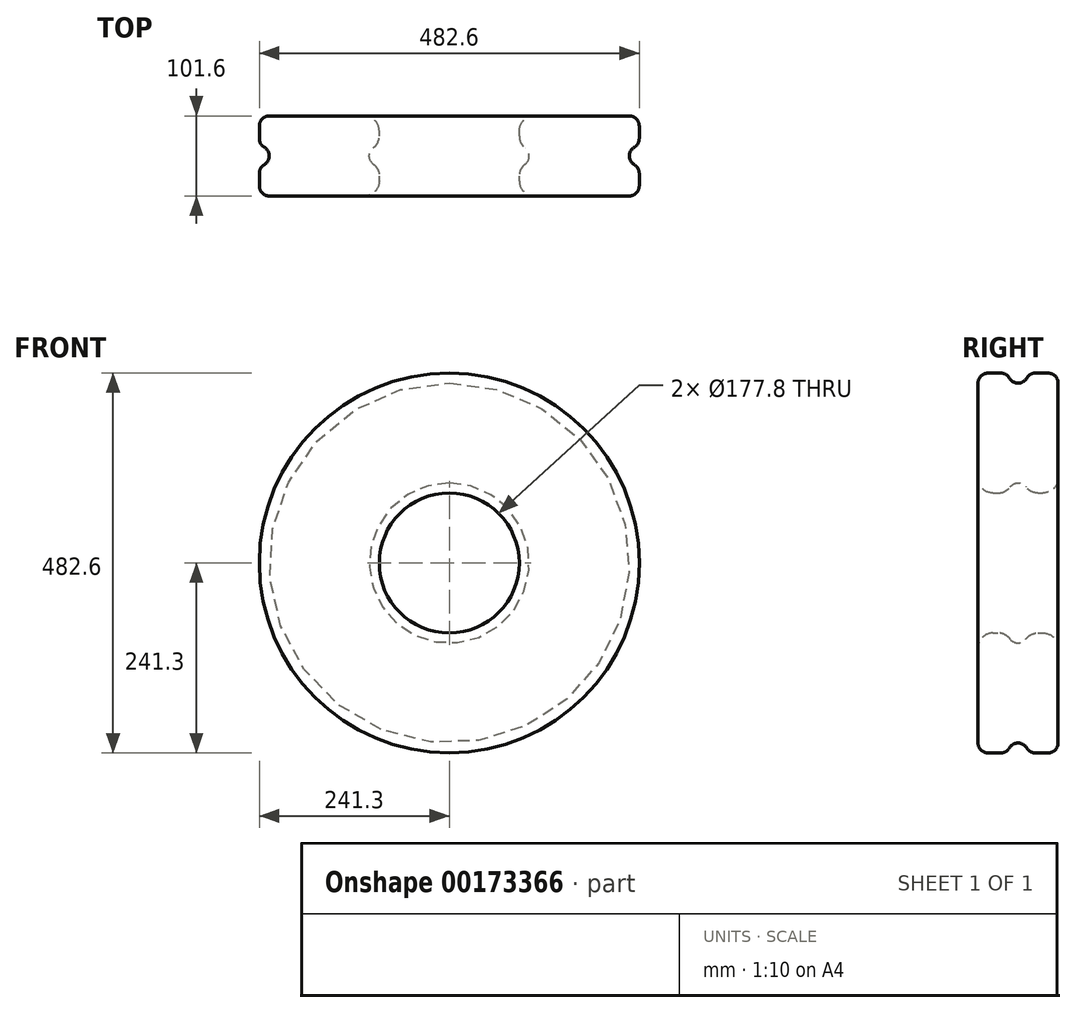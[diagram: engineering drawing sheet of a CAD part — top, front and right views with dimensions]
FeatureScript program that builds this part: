
annotation { "Feature Type Name" : "Feature", "Feature Type Description" : "" }
export const myFeature = defineFeature(function(context is Context, id is Id, definition is map)
    precondition{}
    {
        {
            var Q0;
            Q0=qCreatedBy(makeId("Top.planeOp"),FACE);
            var sketch = newSketch(context, id + "F0", { "sketchPlane" : qUnion([Q0])});
            skLineSegment(sketch, "E0.bottom", {"start": v(88.9, 0) * mm, "end": v(241.3, 0) * mm});
            skLineSegment(sketch, "E0.top", {"start": v(88.9, 101.6) * mm, "end": v(241.3, 101.6) * mm});
            skLineSegment(sketch, "E0.left", {"start": v(88.9, 0) * mm, "end": v(88.9, 38.1) * mm});
            skLineSegment(sketch, "E0.right", {"start": v(241.3, 0) * mm, "end": v(241.3, 38.1) * mm});
            skLineSegment(sketch, "E1", {"start": v(101.6, 50.8) * mm, "end": v(228.6, 50.8) * mm});
            skLineSegment(sketch, "E2", {"start": v(88.9, 38.1) * mm, "end": v(241.3, 38.1) * mm});
            skLineSegment(sketch, "E3", {"start": v(88.9, 63.5) * mm, "end": v(241.3, 63.5) * mm});
            skLineSegment(sketch, "E4", {"start": v(0, 107.57) * mm, "end": v(0, 0) * mm, "construction": true});
            skArc(sketch, "E5", {"start": v(88.9, 38.1) * mm, "mid": v(101.6, 50.8) * mm, "end": v(88.9, 63.5) * mm});
            skArc(sketch, "E6", {"start": v(241.3, 63.5) * mm, "mid": v(228.6, 50.8) * mm, "end": v(241.3, 38.1) * mm});
            skLineSegment(sketch, "E7.trimOffspring", {"start": v(88.9, 63.5) * mm, "end": v(88.9, 101.6) * mm});
            skLineSegment(sketch, "E8.trimOffspring", {"start": v(241.3, 63.5) * mm, "end": v(241.3, 101.6) * mm});
            skSolve(sketch);
        }
        {
            var Q0;
            Q0 = qSketchRegion(id + "F0", true);
            var Q1;
            Q1=sQuery(id+"F0.wireOp",EDGE,"E4");
            revolve(context, id + "F1", {"entities" : qUnion([Q0]), "axis" : qUnion([Q1]), "revolveType" : RevolveType.FULL});
        }
        {
            var Q0;
            Q0=makeQuery(id+"F1.opRevolve","SWEPT_EDGE",EDGE,{"disambiguationData":[OSD([sQuery(id+"F0.wireOp",EDGE,"E3"),sQuery(id+"F0.wireOp",EDGE,"E6"),sQuery(id+"F0.wireOp",EDGE,"E8.trimOffspring")])]});
            var Q1;
            Q1=makeQuery(id+"F1.opRevolve","SWEPT_EDGE",EDGE,{"disambiguationData":[OSD([sQuery(id+"F0.wireOp",EDGE,"E0.top"),sQuery(id+"F0.wireOp",EDGE,"E8.trimOffspring")])]});
            var Q2;
            Q2=makeQuery(id+"F1.opRevolve","SWEPT_EDGE",EDGE,{"disambiguationData":[OSD([sQuery(id+"F0.wireOp",EDGE,"E0.right"),sQuery(id+"F0.wireOp",EDGE,"E2"),sQuery(id+"F0.wireOp",EDGE,"E6")])]});
            var Q3;
            Q3=makeQuery(id+"F1.opRevolve","SWEPT_EDGE",EDGE,{"disambiguationData":[OSD([sQuery(id+"F0.wireOp",EDGE,"E0.bottom"),sQuery(id+"F0.wireOp",EDGE,"E0.right")])]});
            fillet(context, id + "F2", {"entities" : qUnion([Q0, Q1, Q2, Q3]), "radius" : 12.7 * mm, "tangentPropagation" : true, "allowEdgeOverflow" : false});
        }
        {
            var Q0;
            Q0=makeQuery(id+"F1.opRevolve","SWEPT_EDGE",EDGE,{"disambiguationData":[OSD([sQuery(id+"F0.wireOp",EDGE,"E0.top"),sQuery(id+"F0.wireOp",EDGE,"E7.trimOffspring")])]});
            var Q1;
            Q1=makeQuery(id+"F1.opRevolve","SWEPT_EDGE",EDGE,{"disambiguationData":[OSD([sQuery(id+"F0.wireOp",EDGE,"E3"),sQuery(id+"F0.wireOp",EDGE,"E5"),sQuery(id+"F0.wireOp",EDGE,"E7.trimOffspring")])]});
            var Q2;
            Q2=makeQuery(id+"F1.opRevolve","SWEPT_EDGE",EDGE,{"disambiguationData":[OSD([sQuery(id+"F0.wireOp",EDGE,"E0.left"),sQuery(id+"F0.wireOp",EDGE,"E2"),sQuery(id+"F0.wireOp",EDGE,"E5")])]});
            var Q3;
            Q3=makeQuery(id+"F1.opRevolve","SWEPT_EDGE",EDGE,{"disambiguationData":[OSD([sQuery(id+"F0.wireOp",EDGE,"E0.bottom"),sQuery(id+"F0.wireOp",EDGE,"E0.left")])]});
            fillet(context, id + "F3", {"entities" : qUnion([Q0, Q1, Q2, Q3]), "radius" : 19.05 * mm, "tangentPropagation" : true, "allowEdgeOverflow" : false});
        }
    });
